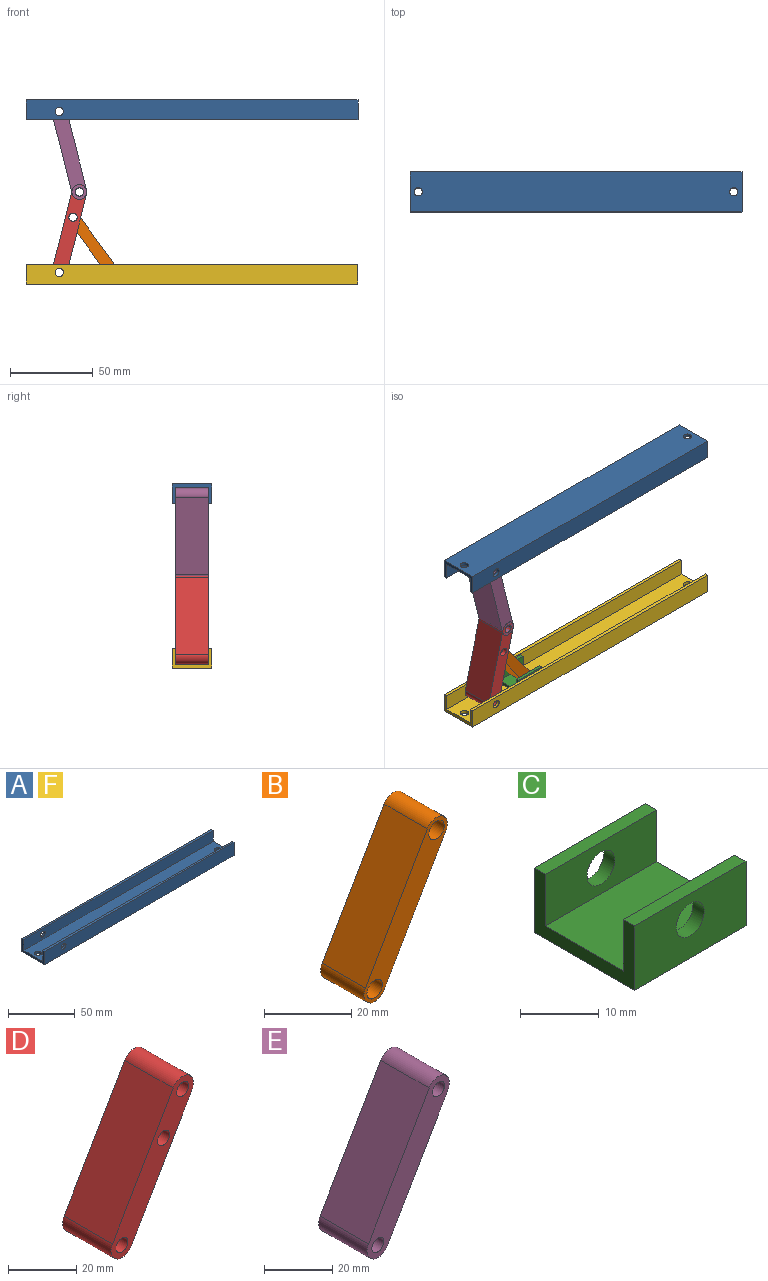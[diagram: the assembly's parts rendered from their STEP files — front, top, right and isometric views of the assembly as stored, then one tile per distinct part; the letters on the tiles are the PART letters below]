
ASSEMBLY  parts=6 mates=7
PART A: 14 faces, bbox 200x24x12 mm
  f0: plane 200x24mm, normal (0,0,-1), area 4760.7mm2, adj f1,f7,f8,f9,f12,f13
  f1: plane 200x12mm, normal (0,1,0), area 2380.4mm2, adj f0,f2,f8,f9,f11
  f2: plane 200x2mm, normal (0,0,1), area 400mm2, adj f1,f3,f8,f9
  f3: plane 200x10mm, normal (0,-1,0), area 1980.4mm2, adj f2,f4,f8,f9,f11
  f4: plane 200x20mm, normal (0,0,1), area 3960.7mm2, adj f3,f5,f8,f9,f12,f13
  f5: plane 200x10mm, normal (0,1,0), area 1980.4mm2, adj f4,f6,f8,f9,f10
  f6: plane 200x2mm, normal (0,0,1), area 400mm2, adj f5,f7,f8,f9
  f7: plane 200x12mm, normal (0,-1,0), area 2380.4mm2, adj f0,f6,f8,f9,f10
  f8: plane 24x12mm, normal (1,0,0), area 88mm2, adj f0,f1,f2,f3,f4,f5,f6,f7
  f9: plane 24x12mm, normal (-1,0,0), area 88mm2, adj f0,f1,f2,f3,f4,f5,f6,f7
  f10: cylinder r=2.5mm len=5mm, axis (0,-1,0), area 31.4mm2, adj f5,f7
  f11: cylinder r=2.5mm len=5mm, axis (0,-1,0), area 31.4mm2, adj f1,f3
  f12: cylinder r=2.5mm len=5mm, axis (0,0,1), area 31.4mm2, adj f0,f4
  f13: cylinder r=2.5mm len=5mm, axis (0,0,1), area 31.4mm2, adj f0,f4
PART B: 8 faces, bbox 27x14x41.6 mm
  f0: cylinder r=3.5mm len=14mm, axis (0,1,0), area 153.9mm2, adj f1,f3,f6,f7
  f1: plane 34.62x20.04mm, normal (-0.87,0,0.5), area 560mm2, adj f0,f2,f6,f7
  f2: cylinder r=3.5mm len=14mm, axis (0,1,0), area 153.9mm2, adj f1,f3,f6,f7
  f3: plane 34.62x20.04mm, normal (0.87,0,-0.5), area 560mm2, adj f0,f2,f6,f7
  f4: cylinder r=2.5mm len=14mm, axis (0,1,0), area 219.9mm2, adj f6,f7
  f5: cylinder r=2.5mm len=14mm, axis (0,1,0), area 219.9mm2, adj f6,f7
  f6: plane 41.62x27.04mm, normal (0,-1,0), area 279.2mm2, adj f0,f1,f2,f3,f4,f5
  f7: plane 41.62x27.04mm, normal (0,1,0), area 279.2mm2, adj f0,f1,f2,f3,f4,f5
PART C: 12 faces, bbox 20x18x10 mm
  f0: plane 20x2mm, normal (0,0,1), area 40mm2, adj f1,f7,f8,f9
  f1: plane 20x10mm, normal (0,1,0), area 180.4mm2, adj f0,f2,f8,f9,f10
  f2: plane 20x18mm, normal (0,0,-1), area 360mm2, adj f1,f3,f8,f9
  f3: plane 20x10mm, normal (0,-1,0), area 180.4mm2, adj f2,f4,f8,f9,f11
  f4: plane 20x2mm, normal (0,0,1), area 40mm2, adj f3,f5,f8,f9
  f5: plane 20x8mm, normal (0,1,0), area 140.4mm2, adj f4,f6,f8,f9,f11
  f6: plane 20x14mm, normal (0,0,1), area 280mm2, adj f5,f7,f8,f9
  f7: plane 20x8mm, normal (0,-1,0), area 140.4mm2, adj f0,f6,f8,f9,f10
  f8: plane 18x10mm, normal (1,0,0), area 68mm2, adj f0,f1,f2,f3,f4,f5,f6,f7
  f9: plane 18x10mm, normal (-1,0,0), area 68mm2, adj f0,f1,f2,f3,f4,f5,f6,f7
  f10: cylinder r=2.5mm len=5mm, axis (0,1,0), area 31.4mm2, adj f1,f7
  f11: cylinder r=2.5mm len=5mm, axis (0,1,0), area 31.4mm2, adj f3,f5
PART D: 9 faces, bbox 34.1x20x52.3 mm
  f0: plane 52.27x34.05mm, normal (0,-1,0), area 454.7mm2, adj f1,f2,f3,f4,f5,f6,f7
  f1: plane 43.27x25.05mm, normal (-0.87,0,0.5), area 1000mm2, adj f0,f2,f6,f8
  f2: cylinder r=4.5mm len=20mm, axis (0,1,0), area 282.7mm2, adj f0,f1,f3,f8
  f3: plane 43.27x25.05mm, normal (0.87,0,-0.5), area 1000mm2, adj f0,f2,f6,f8
  f4: cylinder r=2.5mm len=20mm, axis (0,1,0), area 314.2mm2, adj f0,f8
  f5: cylinder r=2.5mm len=20mm, axis (0,1,0), area 314.2mm2, adj f0,f8
  f6: cylinder r=4.5mm len=20mm, axis (0,1,0), area 282.7mm2, adj f0,f1,f3,f8
  f7: cylinder r=2.5mm len=20mm, axis (0,1,0), area 314.2mm2, adj f0,f8
  f8: plane 52.27x34.05mm, normal (0,1,0), area 454.7mm2, adj f1,f2,f3,f4,f5,f6,f7
PART E: 8 faces, bbox 34.1x20x52.3 mm
  f0: cylinder r=4.5mm len=20mm, axis (0,1,0), area 282.7mm2, adj f1,f3,f6,f7
  f1: plane 43.27x25.05mm, normal (0.87,0,-0.5), area 1000mm2, adj f0,f2,f6,f7
  f2: cylinder r=4.5mm len=20mm, axis (0,1,0), area 282.7mm2, adj f1,f3,f6,f7
  f3: plane 43.27x25.05mm, normal (-0.87,0,0.5), area 1000mm2, adj f0,f2,f6,f7
  f4: cylinder r=2.5mm len=20mm, axis (0,1,0), area 314.2mm2, adj f6,f7
  f5: cylinder r=2.5mm len=20mm, axis (0,1,0), area 314.2mm2, adj f6,f7
  f6: plane 52.27x34.05mm, normal (0,-1,0), area 474.3mm2, adj f0,f1,f2,f3,f4,f5
  f7: plane 52.27x34.05mm, normal (0,1,0), area 474.3mm2, adj f0,f1,f2,f3,f4,f5
PART F: same geometry as A
PLACE A rot(axis=(1,0,0),180deg) t=(-100,4.95,111)mm
PLACE B rot(axis=(0,-1,0),66.2deg) t=(-44.76,-4.95,-4.38)mm
PLACE C t=(-58.05,-4.95,0)mm
PLACE D rot(axis=(0,-1,0),16deg) t=(-97.29,-4.95,-5.25)mm
PLACE E rot(axis=(0,-1,0),44.1deg) t=(-62.93,-4.95,-8.88)mm
PLACE F t=(-100,-4.95,0)mm
MATE slider F.f9 <-> C.f9  axis (-1,0,0) through (-100,0,2)mm
MATE revolute E.f2 <-> A.f10  axis (0,-1,0) through (-80,-10,104)mm
MATE revolute B.f2 <-> C.f10  axis (0,-1,0) through (-48.05,-7,8)mm
MATE revolute E.f0 <-> D.f4  axis (0,1,0) through (-67.85,-10,55.5)mm
MATE slider F.f13 <-> A.f13  axis (0,0,1) through (95,0,2)mm
MATE revolute B.f0 <-> D.f5  axis (0,1,0) through (-71.66,0,40.29)mm
MATE revolute D.f2 <-> F.f10  axis (0,-1,0) through (-80,-10,7)mm
